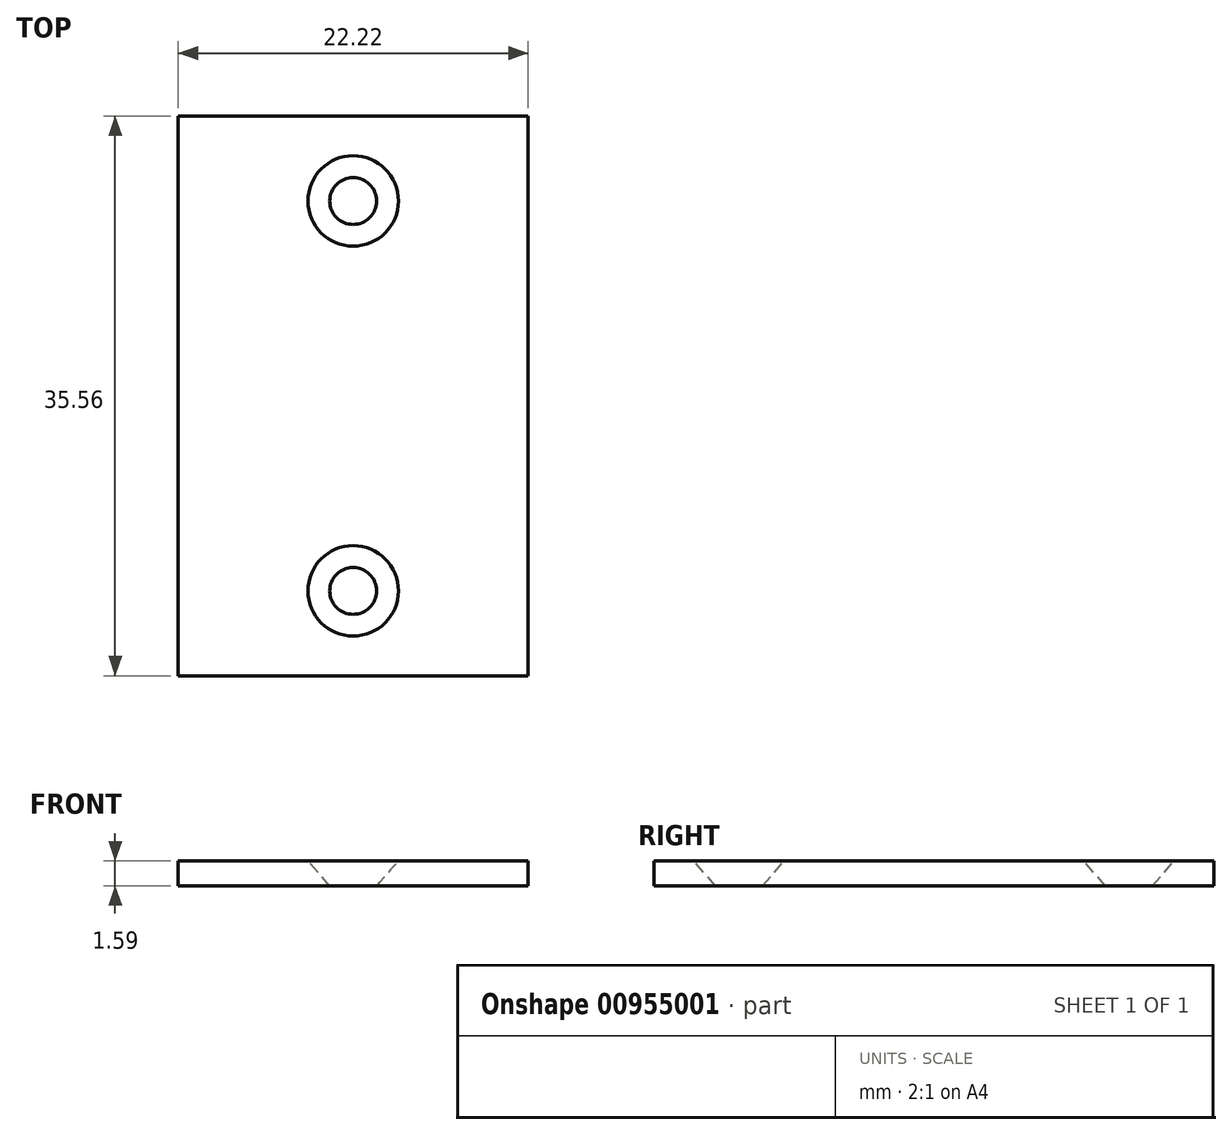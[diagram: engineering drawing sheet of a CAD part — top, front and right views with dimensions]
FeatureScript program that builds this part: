
annotation { "Feature Type Name" : "Feature", "Feature Type Description" : "" }
export const myFeature = defineFeature(function(context is Context, id is Id, definition is map)
    precondition{}
    {
        {
            var Q0;
            Q0=qCreatedBy(makeId("Top.planeOp"),FACE);
            var sketch = newSketch(context, id + "F0", { "sketchPlane" : qUnion([Q0])});
            skLineSegment(sketch, "E0.bottom", {"start": v(-11.11, 17.78) * mm, "end": v(11.11, 17.78) * mm});
            skLineSegment(sketch, "E0.top", {"start": v(-11.11, -17.78) * mm, "end": v(11.11, -17.78) * mm});
            skLineSegment(sketch, "E0.left", {"start": v(-11.11, 17.78) * mm, "end": v(-11.11, -17.78) * mm});
            skLineSegment(sketch, "E0.right", {"start": v(11.11, 17.78) * mm, "end": v(11.11, -17.78) * mm});
            skPoint(sketch, "E0.middle", {"position": v(0, 0) * mm});
            skSolve(sketch);
        }
        {
            var Q0;
            Q0=makeQuery(id+"F0.imprint","IMPRINT",FACE,{"disambiguationData":[TD([[makeQuery(id+"F0.imprint","IMPRINT",EDGE,{"derivedFrom":sQuery(id+"F0.wireOp",EDGE,"E0.bottom")}),-1.0]])]});
            extrude(context, id + "F1", {"entities" : qUnion([Q0]), "depth" : 1.59 * mm, "offsetDistance" : 25.4 * mm});
        }
        {
            var Q0;
            Q0=makeQuery(id+"F1.opExtrude","CAP_FACE",FACE,{"disambiguationData":[OSD([sQuery(id+"F0.wireOp",EDGE,"E0.bottom"),sQuery(id+"F0.wireOp",EDGE,"E0.top"),sQuery(id+"F0.wireOp",EDGE,"E0.left"),sQuery(id+"F0.wireOp",EDGE,"E0.right")])],"isStart":false});
            var sketch = newSketch(context, id + "F2", { "sketchPlane" : qUnion([Q0])});
            skLineSegment(sketch, "E1", {"start": v(0, 12.38) * mm, "end": v(0, -12.38) * mm, "construction": true});
            skSolve(sketch);
        }
        {
            var Q0;
            Q0=sQuery(id+"F2.wireOp",VERTEX,"E1.start");
            var Q1;
            Q1=sQuery(id+"F2.wireOp",VERTEX,"E1.end");
            var Q2;
            Q2=makeQuery(id+"F1.opExtrude","SWEPT_BODY",BODY,{"disambiguationData":[OSD([sQuery(id+"F0.wireOp",EDGE,"E0.bottom"),sQuery(id+"F0.wireOp",EDGE,"E0.top"),sQuery(id+"F0.wireOp",EDGE,"E0.left"),sQuery(id+"F0.wireOp",EDGE,"E0.right")])]});
            hole(context, id + "F3", {"style" : HoleStyle.C_SINK, "endStyle" : HoleEndStyle.THROUGH, "standardTappedOrClearance" : lookupTablePath({ "fit" : "Normal (ASME)", "standard" : "ANSI", "size" : "#3", "type" : "Clearance" }), "standardBlindInLast" : lookupTablePath({ "fit" : "Normal", "standard" : "ANSI", "engagement" : "75%", "pitch" : "48 tpi", "size" : "#3", "type" : "Clearance & tapped" }), "holeDiameter" : 2.95 * mm, "cSinkDiameter" : 5.74 * mm, "cSinkAngle" : 82 * degree, "majorDiameter" : 6.35 * mm, "isTappedThrough" : true, "tappedDepth" : 3.17 * mm, "tapClearance" : 3, "locations" : qUnion([Q0, Q1]), "scope" : qUnion([Q2]), "startStyle" : HoleStartStyle.SKETCH});
        }
    });
